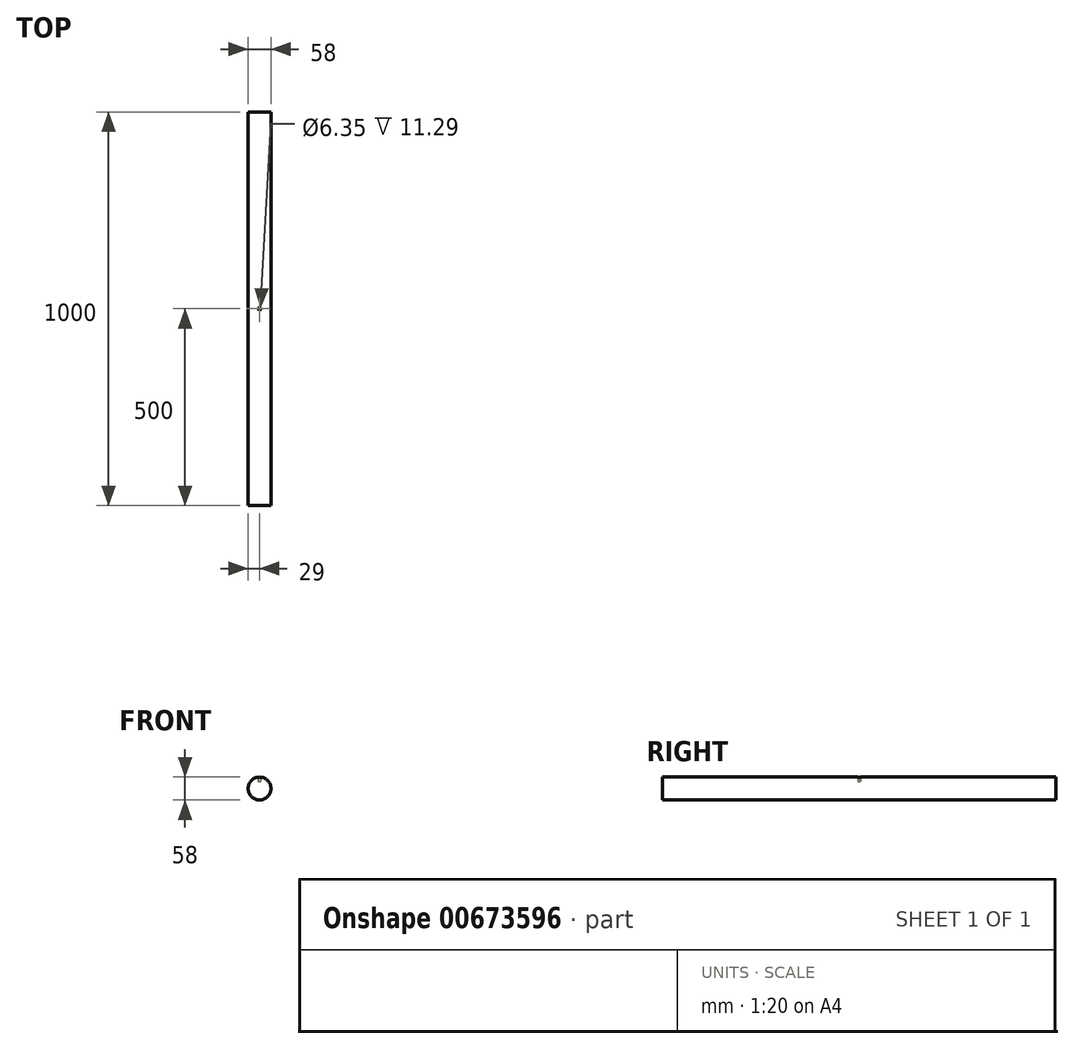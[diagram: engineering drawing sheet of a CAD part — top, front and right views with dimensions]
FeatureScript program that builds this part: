
annotation { "Feature Type Name" : "Feature", "Feature Type Description" : "" }
export const myFeature = defineFeature(function(context is Context, id is Id, definition is map)
    precondition{}
    {
        {
            var Q0;
            Q0=qCreatedBy(makeId("Front.planeOp"),FACE);
            var sketch = newSketch(context, id + "F0", { "sketchPlane" : qUnion([Q0])});
            skCircle(sketch, "E0", {"center": v(0, 0) * mm, "radius": 29 * mm});
            skLineSegment(sketch, "E1.bottom", {"start": v(22.96, 17.71) * mm, "end": v(-22.96, 17.71) * mm});
            skLineSegment(sketch, "E1.top", {"start": v(22.96, -17.71) * mm, "end": v(-22.96, -17.71) * mm});
            skLineSegment(sketch, "E1.left", {"start": v(22.96, 17.71) * mm, "end": v(22.96, -17.71) * mm});
            skLineSegment(sketch, "E1.right", {"start": v(-22.96, 17.71) * mm, "end": v(-22.96, -17.71) * mm});
            skSolve(sketch);
        }
        {
            var Q0;
            Q0=qCreatedBy(makeId("Right.planeOp"),FACE);
            var sketch = newSketch(context, id + "F1", { "sketchPlane" : qUnion([Q0])});
            skLineSegment(sketch, "E2", {"start": v(0, 0) * mm, "end": v(1000, 0) * mm});
            skSolve(sketch);
        }
        {
            var Q0;
            Q0=makeQuery(id+"F0.imprint","IMPRINT",FACE,{"disambiguationData":[TD([[makeQuery(id+"F0.imprint","IMPRINT",EDGE,{"derivedFrom":sQuery(id+"F0.wireOp",EDGE,"E1.bottom")}),1.0]])]});
            extrude(context, id + "F2", {"entities" : qUnion([Q0]), "oppositeDirection" : true, "depth" : 1000 * mm, "offsetDistance" : 25.4 * mm});
        }
        {
            var Q0;
            Q0=makeQuery(id+"F2.opExtrude","SWEPT_FACE",FACE,{"disambiguationData":[OSD([sQuery(id+"F0.wireOp",EDGE,"E1.bottom")])]});
            var sketch = newSketch(context, id + "F3", { "sketchPlane" : qUnion([Q0])});
            skCircle(sketch, "E3", {"center": v(0, 500) * mm, "radius": 3.65 * mm});
            skSolve(sketch);
        }
        {
            var Q0;
            Q0 = qSketchRegion(id + "F0", true);
            extrude(context, id + "F4", {"entities" : qUnion([Q0]), "operationType" : NewBodyOperationType.ADD, "oppositeDirection" : true, "depth" : 1000 * mm, "offsetDistance" : 25.4 * mm});
        }
        {
            var Q0;
            Q0=sQuery(id+"F3.wireOp",VERTEX,"E3.center");
            var Q1;
            Q1=makeQuery(id+"F2.opExtrude","SWEPT_BODY",BODY,{"disambiguationData":[OSD([sQuery(id+"F0.wireOp",EDGE,"E1.bottom"),sQuery(id+"F0.wireOp",EDGE,"E1.top"),sQuery(id+"F0.wireOp",EDGE,"E1.left"),sQuery(id+"F0.wireOp",EDGE,"E1.right")])]});
            hole(context, id + "F5", {"style" : HoleStyle.SIMPLE, "endStyle" : HoleEndStyle.THROUGH, "oppositeDirection" : true, "holeDiameter" : 6.35 * mm, "majorDiameter" : 6.35 * mm, "isTappedThrough" : true, "tappedDepth" : 12.7 * mm, "tapClearance" : 3, "locations" : qUnion([Q0]), "scope" : qUnion([Q1])});
        }
    });
